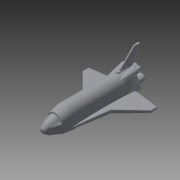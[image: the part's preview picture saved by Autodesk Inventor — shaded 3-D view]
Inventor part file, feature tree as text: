
AUTODESK INVENTOR PART (.ipt)
format: ipt  version: 2015 (Build 190159000, 159)  size: 1,994,752 bytes
history: native  units: in
note: dims shown in document units (in); Inventor stores cm internally (conversion verified against a paired STEP export)
features: sketch x28, plane x14, loft x11, extrude x8, fillet x6, other x3, projected_geometry x3, mirror x2, chamfer x2
ambient origin geometry x8: Origin, YZ Plane, XZ Plane, XY Plane, X Axis, Y Axis, Z Axis, Center Point
bodies: Solid1 (feature_tree)
feature tree (77):
  extrude  "Extrusion1"  TaperAngle=0.0deg  [1 undecoded]
  plane  "Work Plane1"
  plane  "Work Plane2"
  plane  "Work Plane3"
  loft  "Loft1"
  loft  "Loft2"
  fillet  "Fillet1"  Radius=240.6614in
  loft  "Loft4"
  fillet  "Fillet2"  Radius=125.0in
  extrude  "Extrusion2"  TaperAngle=0.0deg  [1 undecoded]
  extrude  "Extrusion3"  Depth=100.0in
  fillet  "Fillet3"  [1 undecoded]
  plane  "Work Plane4"
  mirror  "Mirror1"
  plane  "Work Plane5"
  sketch  "Sketch12"  dims[d36=0.0in d37=90.0deg d38=125.0in]
  loft  "Loft5"
  chamfer  "Chamfer1"  Angle=90.0deg  [1 undecoded]
  chamfer  "Chamfer2"  Angle=90.0deg  [1 undecoded]
  sketch  "Sketch15"  dims[d39=15.0in]
  plane  "Work Plane6"
  plane  "Work Plane7"
  loft  "Loft8"
  mirror  "Mirror2"
  extrude  "Extrusion5"  Depth=125.0in
  extrude  "Extrusion6"  TaperAngle=0.0deg  [1 undecoded]
  plane  "Work Plane8"
  sketch  "Sketch20"  dims[d51=10.0in]
  plane  "Work Plane10"
  loft  "Loft9"
  fillet  "Fillet4"  Radius=84.0in
  extrude  "Extrusion7"  Depth=0.6803in
  fillet  "Fillet5"  Radius=48.0in
  fillet  "Fillet6"  Radius=6500.0in
  sketch  "Sketch23"  dims[d55=0.0in]
  plane  "Work Plane11"
  sketch  "Sketch24"  dims[d56=0.0in]
  loft  "Loft10"
  loft  "Loft11"
  sketch  "Sketch27"  dims[d64=60.0in d70=125.0in]
  plane  "Work Plane12"
  loft  "Loft12"
  loft  "Loft13"
  loft  "Loft14"
  sketch  "Sketch31"  dims[d89=6500.0in d90=7700.0in]
  plane  "Work Plane13"
  sketch  "Sketch32"  dims[d91=10.0in d92=345.0in d93=0.0in]
  sketch  "Sketch33"  dims[d94=10.0in d95=125.0in]
  plane  "Work Plane14"
  extrude  "Extrusion8"  Depth=245.0in
  sketch  "Sketch35"  dims[d98=10.0in d99=0.0in]
  plane  "Work Plane15"
  extrude  "Extrusion9"  Depth=90.0in
  sketch  "Sketch1"  dims[d5=250.0in d12=0.0in]
  sketch  "Sketch2"  dims[d13=75.0in d15=110.0in]
  other  "Edges1"
  sketch  "Sketch3"  dims[d21=98.0in d24=110.0in d25=240.6614in]
  sketch  "Sketch6"  dims[d26=730.0in d27=0.0in d28=300.0in d29=125.0in]
  sketch  "Sketch7"  dims[d30=250.0in d31=0.0in]
  other  "Edges3"
  sketch  "Sketch8"  dims[d32=125.0in d33=100.0in d34=0.0in d35=90.0deg]
  other  "Edges4"
  sketch  "Sketch17"  dims[d40=20.0in]
  sketch  "Sketch18"  dims[d41=10.0in]
  sketch  "Sketch19"  dims[d50=15.0in]
  projected_geometry  "Projected Loop7"
  sketch  "Sketch21"  dims[d52=75.0in]
  sketch  "Sketch22"  dims[d54=125.0in]
  sketch  "Sketch25"  dims[d57=0.0in d58=0.0in d59=90.0deg d60=0.0in d61=90.0deg]
  sketch  "Sketch26"  dims[d62=10.65in d63=50.0in]
  sketch  "Sketch28"  dims[d71=50.0in d72=0.0in d73=90.0deg]
  sketch  "Sketch29"  dims[d74=0.0in d75=90.0deg d76=40.0in d79=84.0in]
  sketch  "Sketch30"  dims[d80=0.0in d82=0.6803in d83=48.0in d84=0.0in d85=6500.0in]
  sketch  "Sketch34"  dims[d96=200.0in d97=0.0in]
  projected_geometry  "Projected Loop8"
  projected_geometry  "Projected Loop9"
  sketch  "Sketch36"  dims[d100=0.0in d101=245.0in d102=90.0in d105=15.0in d106=0.0618in d107=45.0deg d108=345.0in d109=0.0in d110=90.0deg d111=0.0in d112=90.0deg d113=5.2in d114=0.125in d115=45.0deg d116=5.2in d117=0.125in d118=45.0deg d119=-200.0in d126=100.0in d127=25.0in d133=-205.0in d134=50.0in d135=60.0in d137=0.0in d138=90.0deg d139=0.0in d140=90.0deg d141=160.0in d142=100.0in d143=0.6528in d144=0.0in d145=0.0in d146=9000.0in d147=0.0in d148=15.0in d149=25.0in d150=0.0in d151=30.0in d152=0.0in d153=-20.0in d154=30.0in d155=10.0in d156=1.2162in d157=1.2162in d158=195.0in d160=225.0in d166=30.0in d167=225.0in d168=20.0in d169=30.0in d170=20.0in d171=80.0in d172=0.0in d173=90.0deg d174=0.0in d175=90.0deg d176=7.0in d177=0.1374in d178=200.0in d179=0.0in d180=9.475in d184=150.0in d185=150.0in d186=9.475in d187=40.0in d188=80.0in d189=65.0in d190=60.0in d191=20.0in d192=125.0in d193=0.0in d194=13.0in d195=32.0in d196=55.0in d197=55.0in d198=55.0in d199=80.0in d200=95.0in d201=95.0in d202=40.0in d203=0.0in d204=90.0deg d205=0.0in d206=90.0deg d207=0.0in d208=90.0deg d209=0.0in d210=90.0deg d211=25.0in d212=90.0in d213=8.0in d214=0.0in d215=90.0deg d216=0.0in d217=90.0deg d218=105.0in d219=5.0in d220=5.0in d221=0.0in d222=90.0deg d223=0.0in d224=90.0deg d225=105.0in d226=5.0in d227=5.0in d228=0.0in d229=90.0deg d230=0.0in d231=90.0deg d232=-20.0in d233=90.0deg d234=95.0in d235=0.0in d236=90.0deg d237=105.0in d238=0.0in]
note: 6 required parameter values undecoded (feature->parameter linkage not recoverable at this tier; creation-order binding heuristic only, values carry confidence <= 0.55)
